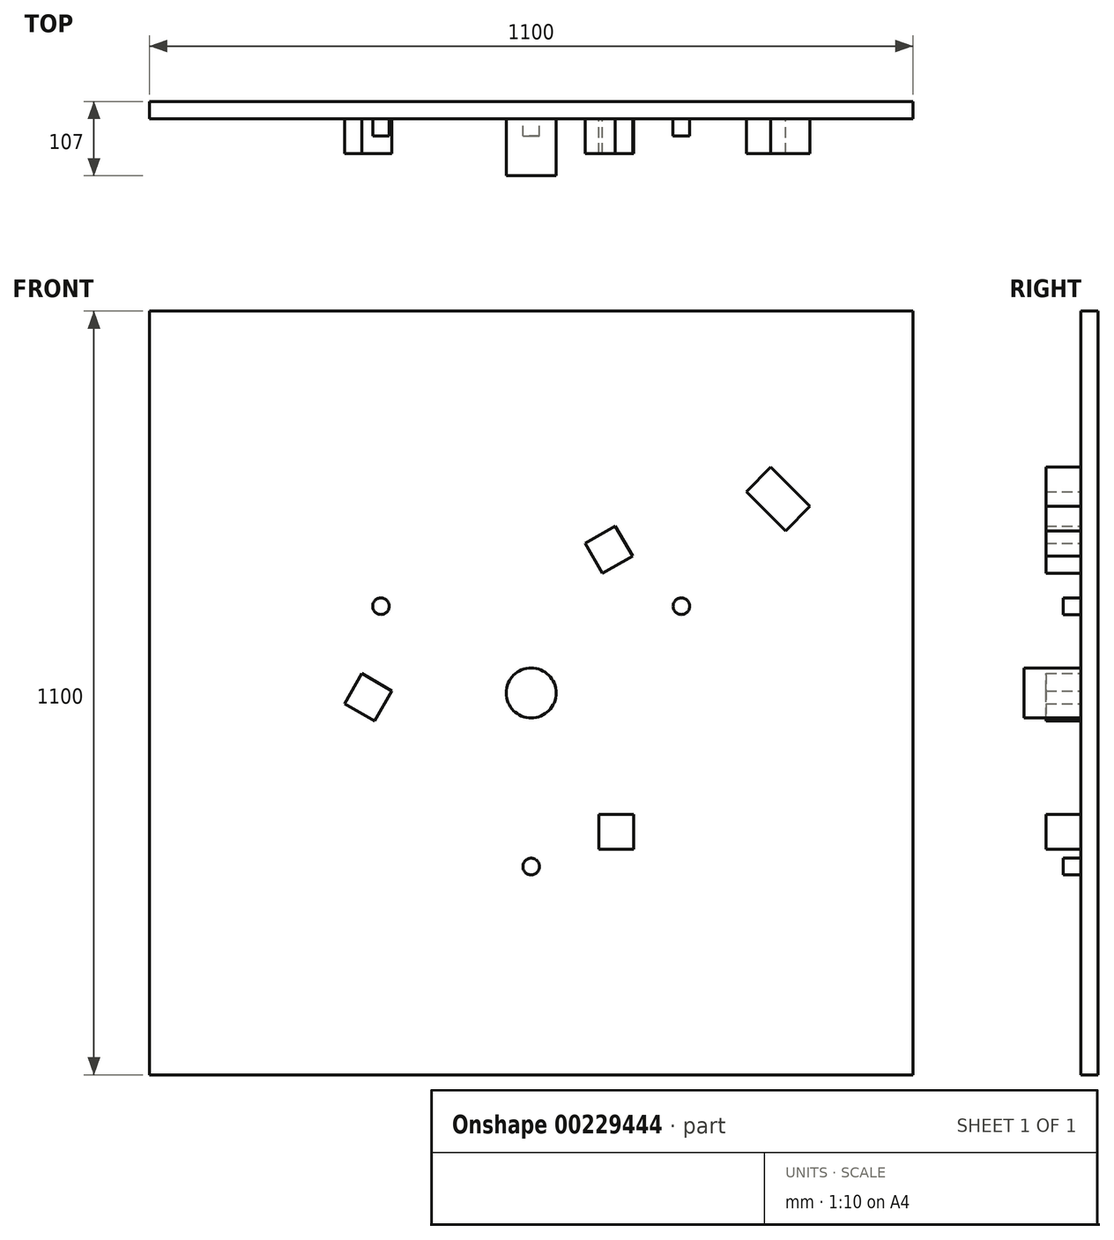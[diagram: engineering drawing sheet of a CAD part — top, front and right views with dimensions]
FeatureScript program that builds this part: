
annotation { "Feature Type Name" : "Feature", "Feature Type Description" : "" }
export const myFeature = defineFeature(function(context is Context, id is Id, definition is map)
    precondition{}
    {
        {
            var Q0;
            Q0=qCreatedBy(makeId("Front.planeOp"),FACE);
            var sketch = newSketch(context, id + "F0", { "sketchPlane" : qUnion([Q0])});
            skLineSegment(sketch, "E0.bottom", {"start": v(550, 550) * mm, "end": v(-550, 550) * mm});
            skLineSegment(sketch, "E0.top", {"start": v(550, -550) * mm, "end": v(-550, -550) * mm});
            skLineSegment(sketch, "E0.left", {"start": v(550, 550) * mm, "end": v(550, -550) * mm});
            skLineSegment(sketch, "E0.right", {"start": v(-550, 550) * mm, "end": v(-550, -550) * mm});
            skPoint(sketch, "E0.middle", {"position": v(0, 0) * mm});
            skSolve(sketch);
        }
        {
            var Q0;
            Q0=makeQuery(id+"F0.imprint","IMPRINT",FACE,{"disambiguationData":[TD([[makeQuery(id+"F0.imprint","IMPRINT",EDGE,{"derivedFrom":sQuery(id+"F0.wireOp",EDGE,"E0.bottom")}),1.0]])]});
            extrude(context, id + "F1", {"entities" : qUnion([Q0]), "depth" : 25 * mm});
        }
        {
            var Q0;
            Q0=makeQuery(id+"F1.opExtrude","CAP_FACE",FACE,{"disambiguationData":[OSD([sQuery(id+"F0.wireOp",EDGE,"E0.bottom"),sQuery(id+"F0.wireOp",EDGE,"E0.top"),sQuery(id+"F0.wireOp",EDGE,"E0.left"),sQuery(id+"F0.wireOp",EDGE,"E0.right")])],"isStart":false});
            var sketch = newSketch(context, id + "F2", { "sketchPlane" : qUnion([Q0])});
            skCircle(sketch, "E1", {"center": v(0, 0) * mm, "radius": 36.01 * mm});
            skSolve(sketch);
        }
        {
            var Q0;
            Q0=makeQuery(id+"F2.imprint","IMPRINT",FACE,{"disambiguationData":[TD([[makeQuery(id+"F2.imprint","IMPRINT",EDGE,{"derivedFrom":sQuery(id+"F2.wireOp",EDGE,"E1")}),1.0]])]});
            extrude(context, id + "F3", {"entities" : qUnion([Q0]), "operationType" : NewBodyOperationType.ADD, "depth" : 82 * mm});
        }
        {
            var Q0;
            Q0=makeQuery(id+"F1.opExtrude","CAP_FACE",FACE,{"disambiguationData":[OSD([sQuery(id+"F0.wireOp",EDGE,"E0.bottom"),sQuery(id+"F0.wireOp",EDGE,"E0.top"),sQuery(id+"F0.wireOp",EDGE,"E0.left"),sQuery(id+"F0.wireOp",EDGE,"E0.right")])],"isStart":false});
            var sketch = newSketch(context, id + "F4", { "sketchPlane" : qUnion([Q0])});
            skLineSegment(sketch, "E2", {"start": v(-69.9, -250) * mm, "end": v(69.9, -250) * mm, "construction": true});
            skLineSegment(sketch, "E3", {"start": v(0, 0) * mm, "end": v(0, -250) * mm, "construction": true});
            skCircle(sketch, "E4", {"center": v(0, -250) * mm, "radius": 12 * mm});
            skPoint(sketch, "E5.center", {"position": v(0, 0) * mm});
            skCircle(sketch, "E6.1.0", {"center": v(216.5, 125) * mm, "radius": 12 * mm});
            skCircle(sketch, "E6.2.0", {"center": v(-216.5, 125) * mm, "radius": 12 * mm});
            skSolve(sketch);
        }
        {
            var Q0;
            Q0=makeQuery(id+"F4.imprint","IMPRINT",FACE,{"disambiguationData":[TD([[makeQuery(id+"F4.imprint","IMPRINT",EDGE,{"derivedFrom":sQuery(id+"F4.wireOp",EDGE,"E4")}),1.0]])]});
            var Q1;
            Q1=makeQuery(id+"F4.imprint","IMPRINT",FACE,{"disambiguationData":[TD([[makeQuery(id+"F4.imprint","IMPRINT",EDGE,{"derivedFrom":sQuery(id+"F4.wireOp",EDGE,"4a09353e-be99-4db0-8383-029719dc8a94.2.0")}),1.0]])]});
            var Q2;
            Q2=makeQuery(id+"F4.imprint","IMPRINT",FACE,{"disambiguationData":[TD([[makeQuery(id+"F4.imprint","IMPRINT",EDGE,{"derivedFrom":sQuery(id+"F4.wireOp",EDGE,"4a09353e-be99-4db0-8383-029719dc8a94.1.0")}),1.0]])]});
            extrude(context, id + "F5", {"entities" : qUnion([Q0, Q1, Q2]), "operationType" : NewBodyOperationType.ADD, "depth" : 25 * mm});
        }
        {
            var Q0;
            Q0=makeQuery(id+"F4.imprint","IMPRINT",FACE,{"disambiguationData":[TD([[makeQuery(id+"F4.imprint","IMPRINT",EDGE,{"derivedFrom":sQuery(id+"F4.wireOp",EDGE,"E6.2.0")}),1.0]])]});
            var Q1;
            Q1=makeQuery(id+"F4.imprint","IMPRINT",FACE,{"disambiguationData":[TD([[makeQuery(id+"F4.imprint","IMPRINT",EDGE,{"derivedFrom":sQuery(id+"F4.wireOp",EDGE,"E6.1.0")}),1.0]])]});
            extrude(context, id + "F6", {"entities" : qUnion([Q0, Q1]), "operationType" : NewBodyOperationType.ADD, "depth" : 25 * mm});
        }
        {
            var Q0;
            Q0=makeQuery(id+"F1.opExtrude","CAP_FACE",FACE,{"disambiguationData":[OSD([sQuery(id+"F0.wireOp",EDGE,"E0.bottom"),sQuery(id+"F0.wireOp",EDGE,"E0.top"),sQuery(id+"F0.wireOp",EDGE,"E0.left"),sQuery(id+"F0.wireOp",EDGE,"E0.right")])],"isStart":false});
            var sketch = newSketch(context, id + "F7", { "sketchPlane" : qUnion([Q0])});
            skCircle(sketch, "E7", {"center": v(0, 0) * mm, "radius": 88.07 * mm, "construction": true});
            skLineSegment(sketch, "E8", {"start": v(196.5, 159.64) * mm, "end": v(236.5, 90.36) * mm, "construction": true});
            skLineSegment(sketch, "E9", {"start": v(236.5, 90.36) * mm, "end": v(402.4, 186.14) * mm, "construction": true});
            skLineSegment(sketch, "E10", {"start": v(402.4, 186.14) * mm, "end": v(362.4, 255.43) * mm, "construction": true});
            skLineSegment(sketch, "E11", {"start": v(362.4, 255.43) * mm, "end": v(196.5, 159.64) * mm, "construction": true});
            skLineSegment(sketch, "E12", {"start": v(77.86, 215.61) * mm, "end": v(102.86, 172.31) * mm});
            skLineSegment(sketch, "E13", {"start": v(102.86, 172.31) * mm, "end": v(146.16, 197.31) * mm});
            skLineSegment(sketch, "E14", {"start": v(146.16, 197.31) * mm, "end": v(121.16, 240.61) * mm});
            skLineSegment(sketch, "E15", {"start": v(121.16, 240.61) * mm, "end": v(77.86, 215.61) * mm});
            skLineSegment(sketch, "E16.1.0", {"start": v(-225.66, -40.38) * mm, "end": v(-200.66, 2.92) * mm});
            skLineSegment(sketch, "E16.1.1", {"start": v(-200.66, 2.92) * mm, "end": v(-243.96, 27.92) * mm});
            skLineSegment(sketch, "E16.1.2", {"start": v(-268.96, -15.38) * mm, "end": v(-225.66, -40.38) * mm});
            skLineSegment(sketch, "E16.1.3", {"start": v(-243.96, 27.92) * mm, "end": v(-268.96, -15.38) * mm});
            skLineSegment(sketch, "E16.2.0", {"start": v(147.8, -175.24) * mm, "end": v(97.8, -175.24) * mm});
            skLineSegment(sketch, "E16.2.1", {"start": v(97.8, -175.24) * mm, "end": v(97.8, -225.24) * mm});
            skLineSegment(sketch, "E16.2.2", {"start": v(147.8, -225.24) * mm, "end": v(147.8, -175.24) * mm});
            skLineSegment(sketch, "E16.2.3", {"start": v(97.8, -225.24) * mm, "end": v(147.8, -225.24) * mm});
            skSolve(sketch);
        }
        {
            var Q0;
            Q0=makeQuery(id+"F7.imprint","IMPRINT",FACE,{"disambiguationData":[TD([[makeQuery(id+"F7.imprint","IMPRINT",EDGE,{"derivedFrom":sQuery(id+"F7.wireOp",EDGE,"E12")}),1.0]])]});
            var Q1;
            Q1=makeQuery(id+"F7.imprint","IMPRINT",FACE,{"disambiguationData":[TD([[makeQuery(id+"F7.imprint","IMPRINT",EDGE,{"derivedFrom":sQuery(id+"F7.wireOp",EDGE,"E16.2.0")}),1.0]])]});
            var Q2;
            Q2=makeQuery(id+"F7.imprint","IMPRINT",FACE,{"disambiguationData":[TD([[makeQuery(id+"F7.imprint","IMPRINT",EDGE,{"derivedFrom":sQuery(id+"F7.wireOp",EDGE,"E16.1.0")}),1.0]])]});
            extrude(context, id + "F8", {"entities" : qUnion([Q0, Q1, Q2]), "operationType" : NewBodyOperationType.ADD, "depth" : 50 * mm});
        }
        {
            var Q0;
            Q0=makeQuery(id+"F1.opExtrude","CAP_FACE",FACE,{"disambiguationData":[OSD([sQuery(id+"F0.wireOp",EDGE,"E0.bottom"),sQuery(id+"F0.wireOp",EDGE,"E0.top"),sQuery(id+"F0.wireOp",EDGE,"E0.left"),sQuery(id+"F0.wireOp",EDGE,"E0.right")])],"isStart":false});
            var sketch = newSketch(context, id + "F9", { "sketchPlane" : qUnion([Q0])});
            skLineSegment(sketch, "E17", {"start": v(310, 290) * mm, "end": v(366.57, 233.43) * mm});
            skLineSegment(sketch, "E18", {"start": v(366.57, 233.43) * mm, "end": v(401.92, 268.79) * mm});
            skLineSegment(sketch, "E19", {"start": v(401.92, 268.79) * mm, "end": v(345.36, 325.36) * mm});
            skLineSegment(sketch, "E20", {"start": v(345.36, 325.36) * mm, "end": v(310, 290) * mm});
            skLineSegment(sketch, "E21", {"start": v(0, 0) * mm, "end": v(374.09, 374.09) * mm, "construction": true});
            skSolve(sketch);
        }
        {
            var Q0;
            Q0=makeQuery(id+"F9.imprint","IMPRINT",FACE,{"disambiguationData":[TD([[makeQuery(id+"F9.imprint","IMPRINT",EDGE,{"derivedFrom":sQuery(id+"F9.wireOp",EDGE,"E17")}),1.0]])]});
            extrude(context, id + "F10", {"entities" : qUnion([Q0]), "operationType" : NewBodyOperationType.ADD, "depth" : 50 * mm});
        }
    });
